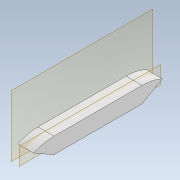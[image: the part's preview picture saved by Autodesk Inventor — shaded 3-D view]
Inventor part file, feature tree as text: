
AUTODESK INVENTOR PART (.ipt)
format: ipt  version: 2021 (Build 250183000, 183)  size: 96,256 bytes
history: native  units: in
note: dims shown in document units (in); Inventor stores cm internally (conversion verified against a paired STEP export)
features: extrude x1, plane x1, sketch x1
ambient origin geometry x8: Origin, YZ Plane, XZ Plane, XY Plane, X Axis, Y Axis, Z Axis, Center Point
bodies: Solid1 (feature_tree)
feature tree (3):
  extrude  "Extrusion1"  Depth=1.0in
  plane  "Work Plane1"
  sketch  "Sketch1"  dims[d0=5.5in d2=6.0in d3=1.0in d4=1.0in d5=1.0in d6=0.0in d7=-0.5in]
